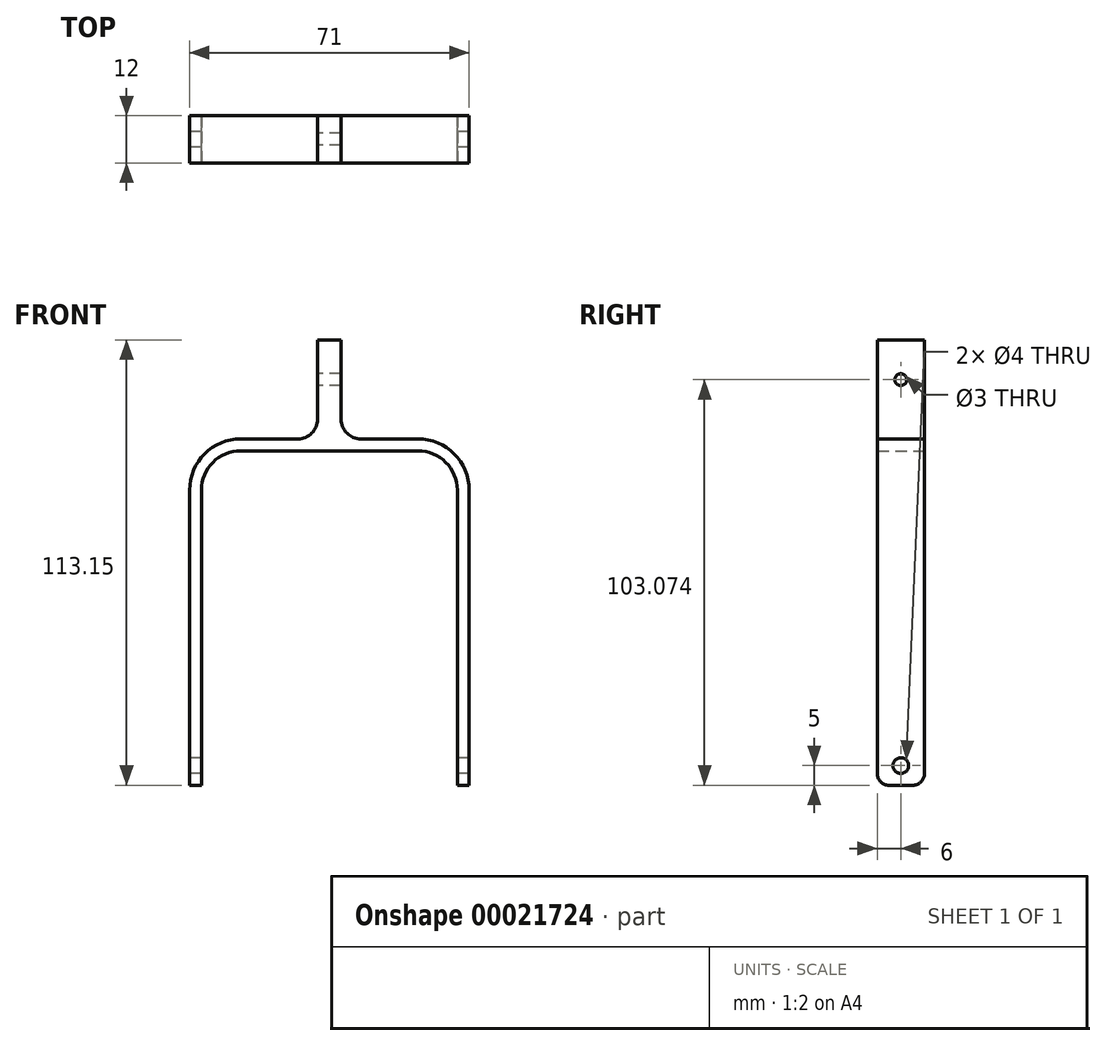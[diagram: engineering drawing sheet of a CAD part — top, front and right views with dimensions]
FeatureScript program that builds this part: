
annotation { "Feature Type Name" : "Feature", "Feature Type Description" : "" }
export const myFeature = defineFeature(function(context is Context, id is Id, definition is map)
    precondition{}
    {
        {
            var Q0;
            Q0=qCreatedBy(makeId("Front.planeOp"),FACE);
            var sketch = newSketch(context, id + "F0", { "sketchPlane" : qUnion([Q0])});
            skCircle(sketch, "E0", {"center": v(0, 0) * mm, "radius": 30 * mm, "construction": true});
            skCircle(sketch, "E1", {"center": v(0, 0) * mm, "radius": 32.5 * mm, "construction": true});
            skLineSegment(sketch, "E2", {"start": v(5, 80) * mm, "end": v(22.5, 80) * mm});
            skLineSegment(sketch, "E3.0", {"start": v(3, 0) * mm, "end": v(3, 108.15) * mm, "construction": true});
            skLineSegment(sketch, "E4", {"start": v(32.5, -5) * mm, "end": v(32.5, 5) * mm});
            skLineSegment(sketch, "E5.rect.top", {"start": v(35.5, -5) * mm, "end": v(32.5, -5) * mm});
            skLineSegment(sketch, "E5.rect.left", {"start": v(35.5, 5) * mm, "end": v(35.5, -5) * mm});
            skPoint(sketch, "E5.rect.middle", {"position": v(32.5, 0) * mm});
            skPoint(sketch, "E5.rect.right.start.orphan", {"position": v(29.5, 5) * mm});
            skPoint(sketch, "E6.orphan", {"position": v(29.5, -5) * mm});
            skLineSegment(sketch, "E7", {"start": v(32.5, 5) * mm, "end": v(32.5, 70) * mm});
            skLineSegment(sketch, "E8", {"start": v(16.25, 107.53) * mm, "end": v(16.25, -93.92) * mm, "construction": true});
            skArc(sketch, "E9.filletArc", {"start": v(32.5, 70) * mm, "mid": v(29.57, 77.07) * mm, "end": v(22.5, 80) * mm});
            skArc(sketch, "E10.filletArc", {"start": v(3, 80.42) * mm, "mid": v(3.98, 80.1) * mm, "end": v(5, 80) * mm});
            skLineSegment(sketch, "E11.0", {"start": v(3, 88) * mm, "end": v(3, 108.15) * mm});
            skLineSegment(sketch, "E11.1", {"start": v(8, 83) * mm, "end": v(22.5, 83) * mm});
            skArc(sketch, "E11.2", {"start": v(35.5, 70) * mm, "mid": v(31.7, 79.2) * mm, "end": v(22.5, 83) * mm});
            skLineSegment(sketch, "E11.3", {"start": v(35.5, 5) * mm, "end": v(35.5, 70) * mm});
            skLineSegment(sketch, "E12", {"start": v(0, 108.15) * mm, "end": v(3, 108.15) * mm});
            skPoint(sketch, "E13.visualSharp", {"position": v(3, 83) * mm});
            skArc(sketch, "E13.filletArc", {"start": v(3, 88) * mm, "mid": v(4.46, 84.46) * mm, "end": v(8, 83) * mm});
            skLineSegment(sketch, "E14.MirrorCS", {"start": v(0, 108.15) * mm, "end": v(-3, 108.15) * mm});
            skLineSegment(sketch, "E15.MirrorCS", {"start": v(-3, 88) * mm, "end": v(-3, 108.15) * mm});
            skArc(sketch, "E16.MirrorCS", {"start": v(-3, 88) * mm, "mid": v(-4.46, 84.46) * mm, "end": v(-8, 83) * mm});
            skLineSegment(sketch, "E17.MirrorCS", {"start": v(-8, 83) * mm, "end": v(-22.5, 83) * mm});
            skLineSegment(sketch, "E18.MirrorCS", {"start": v(-5, 80) * mm, "end": v(-22.5, 80) * mm});
            skArc(sketch, "E19.MirrorCS", {"start": v(-35.5, 70) * mm, "mid": v(-31.7, 79.2) * mm, "end": v(-22.5, 83) * mm});
            skArc(sketch, "E20.MirrorCS", {"start": v(-32.5, 70) * mm, "mid": v(-29.57, 77.07) * mm, "end": v(-22.5, 80) * mm});
            skLineSegment(sketch, "E21.MirrorCS", {"start": v(-32.5, 5) * mm, "end": v(-32.5, 70) * mm});
            skLineSegment(sketch, "E22.MirrorCS", {"start": v(-35.5, 5) * mm, "end": v(-35.5, 70) * mm});
            skLineSegment(sketch, "E23.MirrorCS", {"start": v(-32.5, -5) * mm, "end": v(-32.5, 5) * mm});
            skLineSegment(sketch, "E24.MirrorCS", {"start": v(-35.5, 5) * mm, "end": v(-35.5, -5) * mm});
            skLineSegment(sketch, "E25.MirrorCS", {"start": v(-35.5, -5) * mm, "end": v(-32.5, -5) * mm});
            skLineSegment(sketch, "E26", {"start": v(-5, 80) * mm, "end": v(5, 80) * mm});
            skPoint(sketch, "E27.MirrorCS.start.orphan", {"position": v(0, 85) * mm});
            skSolve(sketch);
        }
        {
            var Q0;
            Q0 = qSketchRegion(id + "F0", true);
            extrude(context, id + "F1", {"entities" : qUnion([Q0]), "depth" : 12 * mm, "symmetric" : true});
        }
        {
            var Q0;
            Q0=makeQuery(id+"F1.opExtrude","SWEPT_FACE",FACE,{"disambiguationData":[OSD([sQuery(id+"F0.wireOp",EDGE,"E22.MirrorCS"),sQuery(id+"F0.wireOp",EDGE,"E24.MirrorCS")])]});
            var sketch = newSketch(context, id + "F2", { "sketchPlane" : qUnion([Q0])});
            skCircle(sketch, "E28", {"center": v(0, 0) * mm, "radius": 2 * mm});
            skSolve(sketch);
        }
        {
            var Q0;
            Q0 = qSketchRegion(id + "F2", true);
            extrude(context, id + "F3", {"entities" : qUnion([Q0]), "operationType" : NewBodyOperationType.REMOVE, "endBound" : BoundingType.THROUGH_ALL, "oppositeDirection" : true, "depth" : 25 * mm});
        }
        {
            var Q0;
            Q0=makeQuery(id+"F1.opExtrude","CAP_EDGE",EDGE,{"disambiguationData":[OSD([sQuery(id+"F0.wireOp",EDGE,"E25.MirrorCS")])],"isStart":true});
            var Q1;
            Q1=makeQuery(id+"F1.opExtrude","CAP_EDGE",EDGE,{"disambiguationData":[OSD([sQuery(id+"F0.wireOp",EDGE,"E25.MirrorCS")])],"isStart":false});
            var Q2;
            Q2=makeQuery(id+"F1.opExtrude","CAP_EDGE",EDGE,{"disambiguationData":[OSD([sQuery(id+"F0.wireOp",EDGE,"E5.rect.top")])],"isStart":true});
            var Q3;
            Q3=makeQuery(id+"F1.opExtrude","CAP_EDGE",EDGE,{"disambiguationData":[OSD([sQuery(id+"F0.wireOp",EDGE,"E5.rect.top")])],"isStart":false});
            fillet(context, id + "F4", {"entities" : qUnion([Q0, Q1, Q2, Q3]), "radius" : 3 * mm, "tangentPropagation" : true, "allowEdgeOverflow" : false});
        }
        {
            var Q0;
            Q0=makeQuery(id+"F1.opExtrude","SWEPT_FACE",FACE,{"disambiguationData":[OSD([sQuery(id+"F0.wireOp",EDGE,"E15.MirrorCS")])]});
            var sketch = newSketch(context, id + "F5", { "sketchPlane" : qUnion([Q0])});
            skLineSegment(sketch, "E29", {"start": v(-6, 98.07) * mm, "end": v(6, 98.07) * mm, "construction": true});
            skLineSegment(sketch, "E30", {"start": v(0, 108.15) * mm, "end": v(0, 88) * mm, "construction": true});
            skCircle(sketch, "E31", {"center": v(0, 98.07) * mm, "radius": 1.5 * mm});
            skSolve(sketch);
        }
        {
            var Q0;
            Q0 = qSketchRegion(id + "F5", true);
            extrude(context, id + "F6", {"entities" : qUnion([Q0]), "operationType" : NewBodyOperationType.REMOVE, "endBound" : BoundingType.UP_TO_NEXT, "oppositeDirection" : true, "depth" : 25 * mm});
        }
    });
